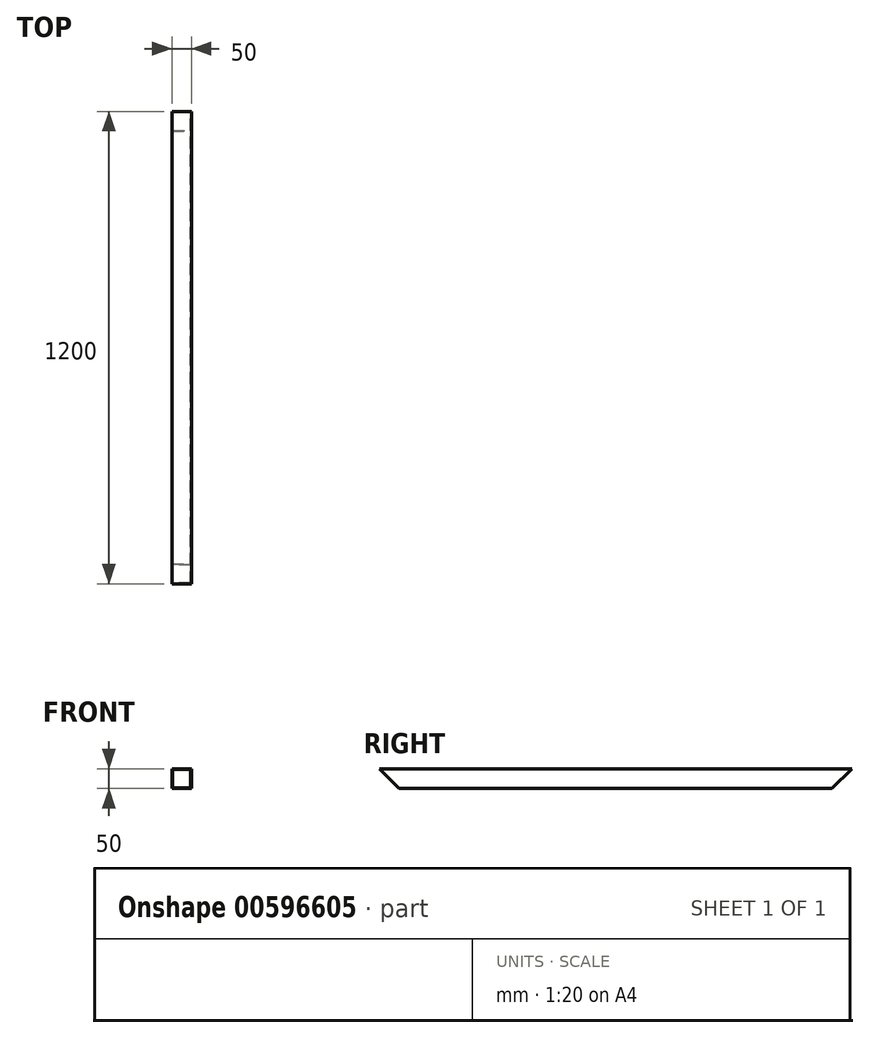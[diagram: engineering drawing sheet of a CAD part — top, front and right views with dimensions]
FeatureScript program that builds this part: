
annotation { "Feature Type Name" : "Feature", "Feature Type Description" : "" }
export const myFeature = defineFeature(function(context is Context, id is Id, definition is map)
    precondition{}
    {
        {
            var Q0;
            Q0=qCreatedBy(makeId("Front.planeOp"),FACE);
            var sketch = newSketch(context, id + "F0", { "sketchPlane" : qUnion([Q0])});
            skLineSegment(sketch, "E0.bottom", {"start": v(0, 0) * mm, "end": v(50, 0) * mm});
            skLineSegment(sketch, "E0.top", {"start": v(0, 50) * mm, "end": v(50, 50) * mm});
            skLineSegment(sketch, "E0.left", {"start": v(0, 0) * mm, "end": v(0, 50) * mm});
            skLineSegment(sketch, "E0.right", {"start": v(50, 0) * mm, "end": v(50, 50) * mm});
            skLineSegment(sketch, "E1.bottom", {"start": v(2, 2) * mm, "end": v(48, 2) * mm});
            skLineSegment(sketch, "E1.top", {"start": v(2, 48) * mm, "end": v(48, 48) * mm});
            skLineSegment(sketch, "E1.left", {"start": v(2, 2) * mm, "end": v(2, 48) * mm});
            skLineSegment(sketch, "E1.right", {"start": v(48, 2) * mm, "end": v(48, 48) * mm});
            skSolve(sketch);
        }
        {
            var Q0;
            Q0 = qSketchRegion(id + "F0", true);
            extrude(context, id + "F1", {"entities" : qUnion([Q0]), "depth" : 1200 * mm, "offsetDistance" : 25 * mm});
        }
        {
            var Q0;
            Q0=makeQuery(id+"F1.opExtrude","SWEPT_FACE",FACE,{"disambiguationData":[OSD([sQuery(id+"F0.wireOp",EDGE,"E0.right")])]});
            var sketch = newSketch(context, id + "F2", { "sketchPlane" : qUnion([Q0])});
            skLineSegment(sketch, "E2", {"start": v(-1200, 50) * mm, "end": v(-1200, 0) * mm});
            skLineSegment(sketch, "E3", {"start": v(-1200, 0) * mm, "end": v(-1150, 0) * mm});
            skLineSegment(sketch, "E4", {"start": v(-1150, 0) * mm, "end": v(-1200, 50) * mm});
            skSolve(sketch);
        }
        {
            var Q0;
            Q0=makeQuery(id+"F2.imprint","IMPRINT",FACE,{"disambiguationData":[TD([[makeQuery(id+"F2.imprint","IMPRINT",EDGE,{"derivedFrom":sQuery(id+"F2.wireOp",EDGE,"E2")}),-1.0]])]});
            extrude(context, id + "F3", {"entities" : qUnion([Q0]), "operationType" : NewBodyOperationType.REMOVE, "endBound" : BoundingType.THROUGH_ALL, "oppositeDirection" : true, "depth" : 25 * mm, "offsetDistance" : 25 * mm});
        }
        {
            var Q0;
            Q0=makeQuery(id+"F1.opExtrude","SWEPT_FACE",FACE,{"disambiguationData":[OSD([sQuery(id+"F0.wireOp",EDGE,"E0.right")])]});
            var sketch = newSketch(context, id + "F4", { "sketchPlane" : qUnion([Q0])});
            skLineSegment(sketch, "E5", {"start": v(-50, 0) * mm, "end": v(0, 0) * mm});
            skLineSegment(sketch, "E6", {"start": v(0, 0) * mm, "end": v(0, 50) * mm});
            skLineSegment(sketch, "E7", {"start": v(0, 50) * mm, "end": v(-50, 0) * mm});
            skSolve(sketch);
        }
        {
            var Q0;
            Q0=makeQuery(id+"F4.imprint","IMPRINT",FACE,{"disambiguationData":[TD([[makeQuery(id+"F4.imprint","IMPRINT",EDGE,{"derivedFrom":sQuery(id+"F4.wireOp",EDGE,"E5")}),1.0]])]});
            extrude(context, id + "F5", {"entities" : qUnion([Q0]), "operationType" : NewBodyOperationType.REMOVE, "endBound" : BoundingType.THROUGH_ALL, "oppositeDirection" : true, "depth" : 25 * mm, "offsetDistance" : 25 * mm});
        }
    });
